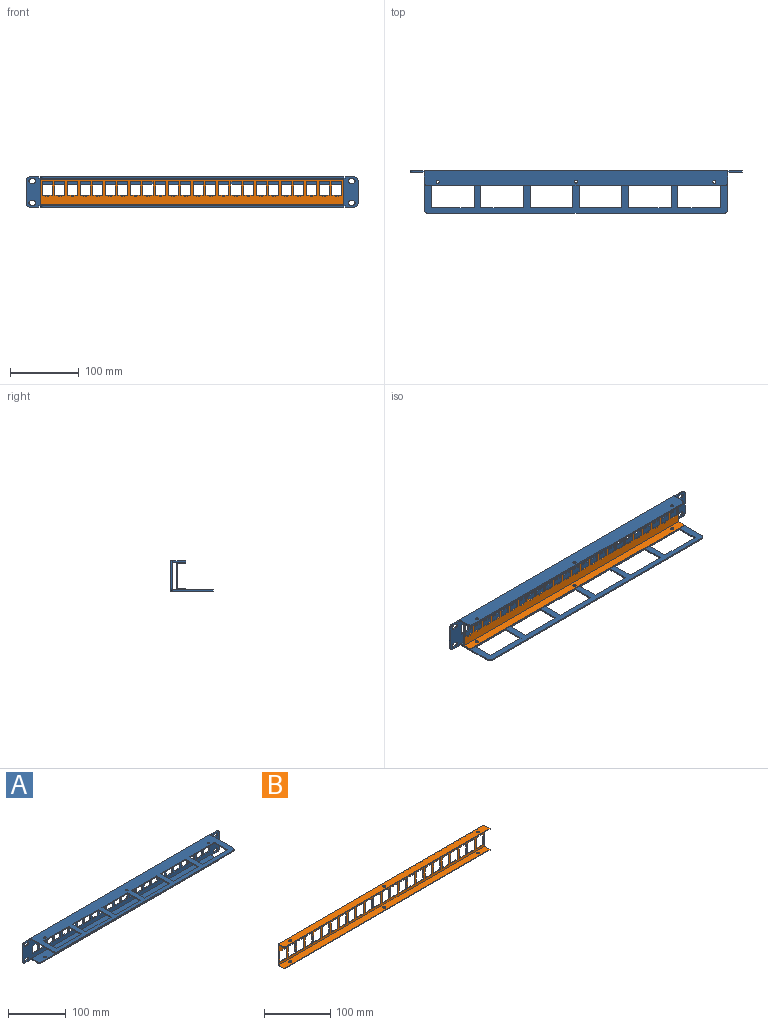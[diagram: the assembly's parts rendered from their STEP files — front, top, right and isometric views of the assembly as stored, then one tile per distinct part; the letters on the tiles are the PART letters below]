
ASSEMBLY  parts=2 mates=1
PART A: 176 faces, bbox 482.7x62x43.8 mm
  f0: plane 440.9x62mm, normal (0,0,1), area 15373.4mm2, adj f86,f87,f134,f143,f144,f145,f146,f147
  f1: plane 440.9x60mm, normal (0,0,-1), area 14491.6mm2, adj f2,f86,f87,f143,f144,f145,f146,f147
  f2: plane 482.7x43.8mm, normal (0,-1,0), area 13415.8mm2, adj f1,f3,f4,f5,f6,f7,f8,f9
  f3: plane 14.65x2mm, normal (0,0,-1), area 29.3mm2, adj f2,f4,f133,f134
  f4: plane 16.2x2mm, normal (-1,0,0), area 32.4mm2, adj f2,f3,f5,f134
  f5: plane 14.65x2mm, normal (0,0,1), area 29.3mm2, adj f2,f4,f133,f134
  f6: plane 14.65x2mm, normal (0,0,-1), area 29.3mm2, adj f2,f7,f105,f134
  f7: plane 16.2x2mm, normal (-1,0,0), area 32.4mm2, adj f2,f6,f8,f134
  f8: plane 14.65x2mm, normal (0,0,1), area 29.3mm2, adj f2,f7,f105,f134
  f9: plane 14.65x2mm, normal (0,0,-1), area 29.3mm2, adj f2,f10,f106,f134
  f10: plane 16.2x2mm, normal (-1,0,0), area 32.4mm2, adj f2,f9,f11,f134
  f11: plane 14.65x2mm, normal (0,0,1), area 29.3mm2, adj f2,f10,f106,f134
  f12: plane 14.65x2mm, normal (0,0,-1), area 29.3mm2, adj f2,f13,f107,f134
  f13: plane 16.2x2mm, normal (-1,0,0), area 32.4mm2, adj f2,f12,f14,f134
  f14: plane 14.65x2mm, normal (0,0,1), area 29.3mm2, adj f2,f13,f107,f134
  f15: plane 14.65x2mm, normal (0,0,-1), area 29.3mm2, adj f2,f16,f108,f134
  f16: plane 16.2x2mm, normal (-1,0,0), area 32.4mm2, adj f2,f15,f17,f134
  f17: plane 14.65x2mm, normal (0,0,1), area 29.3mm2, adj f2,f16,f108,f134
  f18: plane 14.65x2mm, normal (0,0,-1), area 29.3mm2, adj f2,f19,f109,f134
  f19: plane 16.2x2mm, normal (-1,0,0), area 32.4mm2, adj f2,f18,f20,f134
  f20: plane 14.65x2mm, normal (0,0,1), area 29.3mm2, adj f2,f19,f109,f134
  f21: plane 14.65x2mm, normal (0,0,-1), area 29.3mm2, adj f2,f22,f110,f134
  f22: plane 16.2x2mm, normal (-1,0,0), area 32.4mm2, adj f2,f21,f23,f134
  f23: plane 14.65x2mm, normal (0,0,1), area 29.3mm2, adj f2,f22,f110,f134
  f24: plane 14.65x2mm, normal (0,0,-1), area 29.3mm2, adj f2,f25,f111,f134
  f25: plane 16.2x2mm, normal (-1,0,0), area 32.4mm2, adj f2,f24,f26,f134
  f26: plane 14.65x2mm, normal (0,0,1), area 29.3mm2, adj f2,f25,f111,f134
  f27: plane 14.65x2mm, normal (0,0,-1), area 29.3mm2, adj f2,f28,f112,f134
  f28: plane 16.2x2mm, normal (-1,0,0), area 32.4mm2, adj f2,f27,f29,f134
  f29: plane 14.65x2mm, normal (0,0,1), area 29.3mm2, adj f2,f28,f112,f134
  f30: plane 14.65x2mm, normal (0,0,-1), area 29.3mm2, adj f2,f31,f113,f134
  f31: plane 16.2x2mm, normal (-1,0,0), area 32.4mm2, adj f2,f30,f32,f134
  f32: plane 14.65x2mm, normal (0,0,1), area 29.3mm2, adj f2,f31,f113,f134
  f33: plane 14.65x2mm, normal (0,0,-1), area 29.3mm2, adj f2,f34,f114,f134
  f34: plane 16.2x2mm, normal (-1,0,0), area 32.4mm2, adj f2,f33,f35,f134
  f35: plane 14.65x2mm, normal (0,0,1), area 29.3mm2, adj f2,f34,f114,f134
  f36: plane 14.65x2mm, normal (0,0,-1), area 29.3mm2, adj f2,f37,f115,f134
  f37: plane 16.2x2mm, normal (-1,0,0), area 32.4mm2, adj f2,f36,f38,f134
  f38: plane 14.65x2mm, normal (0,0,1), area 29.3mm2, adj f2,f37,f115,f134
  f39: plane 14.65x2mm, normal (0,0,-1), area 29.3mm2, adj f2,f40,f116,f134
  f40: plane 16.2x2mm, normal (-1,0,0), area 32.4mm2, adj f2,f39,f41,f134
  f41: plane 14.65x2mm, normal (0,0,1), area 29.3mm2, adj f2,f40,f116,f134
  f42: plane 14.65x2mm, normal (0,0,-1), area 29.3mm2, adj f2,f43,f117,f134
  f43: plane 16.2x2mm, normal (-1,0,0), area 32.4mm2, adj f2,f42,f44,f134
  f44: plane 14.65x2mm, normal (0,0,1), area 29.3mm2, adj f2,f43,f117,f134
  f45: plane 14.65x2mm, normal (0,0,-1), area 29.3mm2, adj f2,f46,f118,f134
  f46: plane 16.2x2mm, normal (-1,0,0), area 32.4mm2, adj f2,f45,f47,f134
  f47: plane 14.65x2mm, normal (0,0,1), area 29.3mm2, adj f2,f46,f118,f134
  f48: plane 14.65x2mm, normal (0,0,-1), area 29.3mm2, adj f2,f49,f119,f134
  f49: plane 16.2x2mm, normal (-1,0,0), area 32.4mm2, adj f2,f48,f50,f134
  f50: plane 14.65x2mm, normal (0,0,1), area 29.3mm2, adj f2,f49,f119,f134
  f51: plane 14.65x2mm, normal (0,0,-1), area 29.3mm2, adj f2,f52,f120,f134
  f52: plane 16.2x2mm, normal (-1,0,0), area 32.4mm2, adj f2,f51,f53,f134
  f53: plane 14.65x2mm, normal (0,0,1), area 29.3mm2, adj f2,f52,f120,f134
  f54: plane 14.65x2mm, normal (0,0,-1), area 29.3mm2, adj f2,f55,f121,f134
  f55: plane 16.2x2mm, normal (-1,0,0), area 32.4mm2, adj f2,f54,f56,f134
  f56: plane 14.65x2mm, normal (0,0,1), area 29.3mm2, adj f2,f55,f121,f134
  f57: plane 14.65x2mm, normal (0,0,-1), area 29.3mm2, adj f2,f58,f122,f134
  f58: plane 16.2x2mm, normal (-1,0,0), area 32.4mm2, adj f2,f57,f59,f134
  f59: plane 14.65x2mm, normal (0,0,1), area 29.3mm2, adj f2,f58,f122,f134
  f60: plane 14.65x2mm, normal (0,0,-1), area 29.3mm2, adj f2,f61,f123,f134
  f61: plane 16.2x2mm, normal (-1,0,0), area 32.4mm2, adj f2,f60,f62,f134
  f62: plane 14.65x2mm, normal (0,0,1), area 29.3mm2, adj f2,f61,f123,f134
  f63: plane 14.65x2mm, normal (0,0,-1), area 29.3mm2, adj f2,f64,f124,f134
  f64: plane 16.2x2mm, normal (-1,0,0), area 32.4mm2, adj f2,f63,f65,f134
  f65: plane 14.65x2mm, normal (0,0,1), area 29.3mm2, adj f2,f64,f124,f134
  f66: plane 14.65x2mm, normal (0,0,-1), area 29.3mm2, adj f2,f67,f125,f134
  f67: plane 16.2x2mm, normal (-1,0,0), area 32.4mm2, adj f2,f66,f68,f134
  f68: plane 14.65x2mm, normal (0,0,1), area 29.3mm2, adj f2,f67,f125,f134
  f69: plane 14.65x2mm, normal (0,0,-1), area 29.3mm2, adj f2,f70,f126,f134
  f70: plane 16.2x2mm, normal (-1,0,0), area 32.4mm2, adj f2,f69,f71,f134
  f71: plane 14.65x2mm, normal (0,0,1), area 29.3mm2, adj f2,f70,f126,f134
  f72: plane 16.2x2mm, normal (-1,0,0), area 32.4mm2, adj f2,f73,f127,f134
  f73: plane 14.65x2mm, normal (0,0,1), area 29.3mm2, adj f2,f72,f74,f134
  f74: plane 16.2x2mm, normal (1,0,0), area 32.4mm2, adj f2,f73,f127,f134
  f75: cylinder r=3.35mm len=6.7mm, axis (0,-1,0), area 21mm2, adj f2,f76,f128,f134
  f76: plane 3.3x2mm, normal (0,0,-1), area 6.6mm2, adj f2,f75,f77,f134
  f77: cylinder r=3.35mm len=6.7mm, axis (0,-1,0), area 21mm2, adj f2,f76,f128,f134
  f78: cylinder r=3.35mm len=6.7mm, axis (0,-1,0), area 21mm2, adj f2,f79,f129,f134
  f79: plane 3.3x2mm, normal (0,0,-1), area 6.6mm2, adj f2,f78,f80,f134
  f80: cylinder r=3.35mm len=6.7mm, axis (0,-1,0), area 21mm2, adj f2,f79,f129,f134
  f81: plane 13.9x2mm, normal (0,0,-1), area 27.8mm2, adj f2,f130,f134,f139
  f82: plane 33.8x2mm, normal (1,0,0), area 67.6mm2, adj f2,f134,f139,f140
  f83: plane 13.9x2mm, normal (0,0,1), area 27.8mm2, adj f2,f84,f134,f140
  f84: plane 2x2mm, normal (-1,0,0), area 4mm2, adj f2,f83,f85,f134
  f85: plane 2x2mm, normal (0,0,1), area 4mm2, adj f2,f84,f86,f134
  f86: plane 57x2mm, normal (1,0,0), area 114mm2, adj f0,f1,f85,f134,f145
  f87: plane 57x2mm, normal (-1,0,0), area 114mm2, adj f0,f1,f88,f134,f144
  f88: plane 2x2mm, normal (0,0,1), area 4mm2, adj f2,f87,f89,f134
  f89: plane 2x2mm, normal (1,0,0), area 4mm2, adj f2,f88,f90,f134
  f90: plane 13.9x2mm, normal (0,0,1), area 27.8mm2, adj f2,f89,f134,f141
  f91: plane 33.8x2mm, normal (-1,0,0), area 67.6mm2, adj f2,f134,f141,f142
  f92: plane 13.9x2mm, normal (0,0,-1), area 27.8mm2, adj f2,f93,f134,f142
  f93: plane 2x2mm, normal (1,0,0), area 4mm2, adj f2,f92,f94,f134
  f94: plane 2x2mm, normal (0,0,-1), area 4mm2, adj f2,f93,f95,f134
  f95: plane 17x2mm, normal (-1,0,0), area 34mm2, adj f94,f96,f134,f135,f137
  f96: plane 440.9x22mm, normal (0,0,-1), area 9641.4mm2, adj f95,f97,f134,f136,f137,f138,f170,f171
  f97: plane 17x2mm, normal (1,0,0), area 34mm2, adj f96,f98,f134,f135,f138
  f98: plane 2x2mm, normal (0,0,-1), area 4mm2, adj f2,f97,f130,f134
  f99: cylinder r=3.35mm len=6.7mm, axis (0,-1,0), area 21mm2, adj f2,f100,f131,f134
  f100: plane 3.3x2mm, normal (0,0,1), area 6.6mm2, adj f2,f99,f101,f134
  f101: cylinder r=3.35mm len=6.7mm, axis (0,-1,0), area 21mm2, adj f2,f100,f131,f134
  f102: cylinder r=3.35mm len=6.7mm, axis (0,-1,0), area 21mm2, adj f2,f103,f132,f134
  f103: plane 3.3x2mm, normal (0,0,1), area 6.6mm2, adj f2,f102,f104,f134
  f104: cylinder r=3.35mm len=6.7mm, axis (0,-1,0), area 21mm2, adj f2,f103,f132,f134
  f105: plane 16.2x2mm, normal (1,0,0), area 32.4mm2, adj f2,f6,f8,f134
  f106: plane 16.2x2mm, normal (1,0,0), area 32.4mm2, adj f2,f9,f11,f134
  f107: plane 16.2x2mm, normal (1,0,0), area 32.4mm2, adj f2,f12,f14,f134
  f108: plane 16.2x2mm, normal (1,0,0), area 32.4mm2, adj f2,f15,f17,f134
  f109: plane 16.2x2mm, normal (1,0,0), area 32.4mm2, adj f2,f18,f20,f134
  f110: plane 16.2x2mm, normal (1,0,0), area 32.4mm2, adj f2,f21,f23,f134
  f111: plane 16.2x2mm, normal (1,0,0), area 32.4mm2, adj f2,f24,f26,f134
  f112: plane 16.2x2mm, normal (1,0,0), area 32.4mm2, adj f2,f27,f29,f134
  f113: plane 16.2x2mm, normal (1,0,0), area 32.4mm2, adj f2,f30,f32,f134
  f114: plane 16.2x2mm, normal (1,0,0), area 32.4mm2, adj f2,f33,f35,f134
  f115: plane 16.2x2mm, normal (1,0,0), area 32.4mm2, adj f2,f36,f38,f134
  f116: plane 16.2x2mm, normal (1,0,0), area 32.4mm2, adj f2,f39,f41,f134
  f117: plane 16.2x2mm, normal (1,0,0), area 32.4mm2, adj f2,f42,f44,f134
  f118: plane 16.2x2mm, normal (1,0,0), area 32.4mm2, adj f2,f45,f47,f134
  f119: plane 16.2x2mm, normal (1,0,0), area 32.4mm2, adj f2,f48,f50,f134
  f120: plane 16.2x2mm, normal (1,0,0), area 32.4mm2, adj f2,f51,f53,f134
  f121: plane 16.2x2mm, normal (1,0,0), area 32.4mm2, adj f2,f54,f56,f134
  f122: plane 16.2x2mm, normal (1,0,0), area 32.4mm2, adj f2,f57,f59,f134
  f123: plane 16.2x2mm, normal (1,0,0), area 32.4mm2, adj f2,f60,f62,f134
  f124: plane 16.2x2mm, normal (1,0,0), area 32.4mm2, adj f2,f63,f65,f134
  f125: plane 16.2x2mm, normal (1,0,0), area 32.4mm2, adj f2,f66,f68,f134
  f126: plane 16.2x2mm, normal (1,0,0), area 32.4mm2, adj f2,f69,f71,f134
  f127: plane 14.65x2mm, normal (0,0,-1), area 29.3mm2, adj f2,f72,f74,f134
  f128: plane 3.3x2mm, normal (0,0,1), area 6.6mm2, adj f2,f75,f77,f134
  f129: plane 3.3x2mm, normal (0,0,1), area 6.6mm2, adj f2,f78,f80,f134
  f130: plane 2x2mm, normal (-1,0,0), area 4mm2, adj f2,f81,f98,f134
  f131: plane 3.3x2mm, normal (0,0,-1), area 6.6mm2, adj f2,f99,f101,f134
  f132: plane 3.3x2mm, normal (0,0,-1), area 6.6mm2, adj f2,f102,f104,f134
  f133: plane 16.2x2mm, normal (1,0,0), area 32.4mm2, adj f2,f3,f5,f134
  f134: plane 482.7x43.8mm, normal (0,1,0), area 15179.4mm2, adj f0,f3,f4,f5,f6,f7,f8,f9
  f135: plane 440.9x20mm, normal (0,0,1), area 8759.6mm2, adj f2,f95,f97,f136,f137,f138,f170,f171
  f136: plane 430.9x2mm, normal (0,-1,0), area 861.8mm2, adj f96,f135,f137,f138
  f137: cylinder r=5mm len=5mm, axis (0,0,-1), area 15.7mm2, adj f95,f96,f135,f136
  f138: cylinder r=5mm len=5mm, axis (0,0,1), area 15.7mm2, adj f96,f97,f135,f136
  f139: cylinder r=5mm len=5mm, axis (0,-1,0), area 15.7mm2, adj f2,f81,f82,f134
  f140: cylinder r=5mm len=5mm, axis (0,1,0), area 15.7mm2, adj f2,f82,f83,f134
  f141: cylinder r=5mm len=5mm, axis (0,-1,0), area 15.7mm2, adj f2,f90,f91,f134
  f142: cylinder r=5mm len=5mm, axis (0,1,0), area 15.7mm2, adj f2,f91,f92,f134
  f143: plane 430.9x2mm, normal (0,-1,0), area 861.8mm2, adj f0,f1,f144,f145
  f144: cylinder r=5mm len=5mm, axis (0,0,-1), area 15.7mm2, adj f0,f1,f87,f143
  f145: cylinder r=5mm len=5mm, axis (0,0,1), area 15.7mm2, adj f0,f1,f86,f143
  f146: plane 62x2mm, normal (0,-1,0), area 124mm2, adj f0,f1,f147,f149
  f147: plane 32x2mm, normal (-1,0,0), area 64mm2, adj f0,f1,f146,f148
  f148: plane 62x2mm, normal (0,1,0), area 124mm2, adj f0,f1,f147,f149
  f149: plane 32x2mm, normal (1,0,0), area 64mm2, adj f0,f1,f146,f148
  f150: plane 62x2mm, normal (0,-1,0), area 124mm2, adj f0,f1,f151,f153
  f151: plane 32x2mm, normal (-1,0,0), area 64mm2, adj f0,f1,f150,f152
  f152: plane 62x2mm, normal (0,1,0), area 124mm2, adj f0,f1,f151,f153
  f153: plane 32x2mm, normal (1,0,0), area 64mm2, adj f0,f1,f150,f152
  f154: plane 62x2mm, normal (0,-1,0), area 124mm2, adj f0,f1,f155,f157
  f155: plane 32x2mm, normal (-1,0,0), area 64mm2, adj f0,f1,f154,f156
  f156: plane 62x2mm, normal (0,1,0), area 124mm2, adj f0,f1,f155,f157
  f157: plane 32x2mm, normal (1,0,0), area 64mm2, adj f0,f1,f154,f156
  f158: plane 62x2mm, normal (0,-1,0), area 124mm2, adj f0,f1,f159,f161
  f159: plane 32x2mm, normal (-1,0,0), area 64mm2, adj f0,f1,f158,f160
  f160: plane 62x2mm, normal (0,1,0), area 124mm2, adj f0,f1,f159,f161
  f161: plane 32x2mm, normal (1,0,0), area 64mm2, adj f0,f1,f158,f160
  f162: plane 62x2mm, normal (0,-1,0), area 124mm2, adj f0,f1,f163,f165
  f163: plane 32x2mm, normal (-1,0,0), area 64mm2, adj f0,f1,f162,f164
  f164: plane 62x2mm, normal (0,1,0), area 124mm2, adj f0,f1,f163,f165
  f165: plane 32x2mm, normal (1,0,0), area 64mm2, adj f0,f1,f162,f164
  f166: plane 62x2mm, normal (0,-1,0), area 124mm2, adj f0,f1,f167,f169
  f167: plane 32x2mm, normal (-1,0,0), area 64mm2, adj f0,f1,f166,f168
  f168: plane 62x2mm, normal (0,1,0), area 124mm2, adj f0,f1,f167,f169
  f169: plane 32x2mm, normal (1,0,0), area 64mm2, adj f0,f1,f166,f168
  f170: cylinder r=2.25mm len=4.5mm, axis (0,0,1), area 28.3mm2, adj f96,f135
  f171: cylinder r=2.25mm len=4.5mm, axis (0,0,1), area 28.3mm2, adj f96,f135
  f172: cylinder r=2.25mm len=4.5mm, axis (0,0,1), area 28.3mm2, adj f96,f135
  f173: cylinder r=2.25mm len=4.5mm, axis (0,0,1), area 28.3mm2, adj f0,f1
  f174: cylinder r=2.25mm len=4.5mm, axis (0,0,1), area 28.3mm2, adj f0,f1
  f175: cylinder r=2.25mm len=4.5mm, axis (0,0,1), area 28.3mm2, adj f0,f1
PART B: 209 faces, bbox 440.9x13x39.8 mm
  f0: plane 440.9x37.8mm, normal (0,-1,0), area 9613.1mm2, adj f1,f2,f3,f4,f5,f6,f7,f8
  f1: plane 4x1mm, normal (0,0,-1), area 4mm2, adj f0,f2,f196,f197
  f2: plane 1.5x1mm, normal (-1,0,0), area 1.5mm2, adj f0,f1,f3,f197
  f3: plane 5.33x1mm, normal (0,0,-1), area 5.3mm2, adj f0,f2,f4,f197
  f4: plane 19.65x1mm, normal (-1,0,0), area 19.7mm2, adj f0,f3,f5,f197
  f5: plane 14.65x1mm, normal (0,0,1), area 14.6mm2, adj f0,f4,f6,f197
  f6: plane 19.65x1mm, normal (1,0,0), area 19.7mm2, adj f0,f5,f7,f197
  f7: plane 5.33x1mm, normal (0,0,-1), area 5.3mm2, adj f0,f6,f196,f197
  f8: plane 5.33x1mm, normal (0,0,-1), area 5.3mm2, adj f0,f9,f172,f197
  f9: plane 1.5x1mm, normal (1,0,0), area 1.5mm2, adj f0,f8,f10,f197
  f10: plane 4x1mm, normal (0,0,-1), area 4mm2, adj f0,f9,f11,f197
  f11: plane 1.5x1mm, normal (-1,0,0), area 1.5mm2, adj f0,f10,f12,f197
  f12: plane 5.33x1mm, normal (0,0,-1), area 5.3mm2, adj f0,f11,f13,f197
  f13: plane 19.65x1mm, normal (-1,0,0), area 19.7mm2, adj f0,f12,f14,f197
  f14: plane 14.65x1mm, normal (0,0,1), area 14.6mm2, adj f0,f13,f172,f197
  f15: plane 5.33x1mm, normal (0,0,-1), area 5.3mm2, adj f0,f16,f173,f197
  f16: plane 1.5x1mm, normal (1,0,0), area 1.5mm2, adj f0,f15,f17,f197
  f17: plane 4x1mm, normal (0,0,-1), area 4mm2, adj f0,f16,f18,f197
  f18: plane 1.5x1mm, normal (-1,0,0), area 1.5mm2, adj f0,f17,f19,f197
  f19: plane 5.33x1mm, normal (0,0,-1), area 5.3mm2, adj f0,f18,f20,f197
  f20: plane 19.65x1mm, normal (-1,0,0), area 19.7mm2, adj f0,f19,f21,f197
  f21: plane 14.65x1mm, normal (0,0,1), area 14.6mm2, adj f0,f20,f173,f197
  f22: plane 5.33x1mm, normal (0,0,-1), area 5.3mm2, adj f0,f23,f174,f197
  f23: plane 1.5x1mm, normal (1,0,0), area 1.5mm2, adj f0,f22,f24,f197
  f24: plane 4x1mm, normal (0,0,-1), area 4mm2, adj f0,f23,f25,f197
  f25: plane 1.5x1mm, normal (-1,0,0), area 1.5mm2, adj f0,f24,f26,f197
  f26: plane 5.33x1mm, normal (0,0,-1), area 5.3mm2, adj f0,f25,f27,f197
  f27: plane 19.65x1mm, normal (-1,0,0), area 19.7mm2, adj f0,f26,f28,f197
  f28: plane 14.65x1mm, normal (0,0,1), area 14.6mm2, adj f0,f27,f174,f197
  f29: plane 5.33x1mm, normal (0,0,-1), area 5.3mm2, adj f0,f30,f175,f197
  f30: plane 1.5x1mm, normal (1,0,0), area 1.5mm2, adj f0,f29,f31,f197
  f31: plane 4x1mm, normal (0,0,-1), area 4mm2, adj f0,f30,f32,f197
  f32: plane 1.5x1mm, normal (-1,0,0), area 1.5mm2, adj f0,f31,f33,f197
  f33: plane 5.33x1mm, normal (0,0,-1), area 5.3mm2, adj f0,f32,f34,f197
  f34: plane 19.65x1mm, normal (-1,0,0), area 19.7mm2, adj f0,f33,f35,f197
  f35: plane 14.65x1mm, normal (0,0,1), area 14.6mm2, adj f0,f34,f175,f197
  f36: plane 5.33x1mm, normal (0,0,-1), area 5.3mm2, adj f0,f37,f176,f197
  f37: plane 1.5x1mm, normal (1,0,0), area 1.5mm2, adj f0,f36,f38,f197
  f38: plane 4x1mm, normal (0,0,-1), area 4mm2, adj f0,f37,f39,f197
  f39: plane 1.5x1mm, normal (-1,0,0), area 1.5mm2, adj f0,f38,f40,f197
  f40: plane 5.33x1mm, normal (0,0,-1), area 5.3mm2, adj f0,f39,f41,f197
  f41: plane 19.65x1mm, normal (-1,0,0), area 19.7mm2, adj f0,f40,f42,f197
  f42: plane 14.65x1mm, normal (0,0,1), area 14.6mm2, adj f0,f41,f176,f197
  f43: plane 5.33x1mm, normal (0,0,-1), area 5.3mm2, adj f0,f44,f177,f197
  f44: plane 1.5x1mm, normal (1,0,0), area 1.5mm2, adj f0,f43,f45,f197
  f45: plane 4x1mm, normal (0,0,-1), area 4mm2, adj f0,f44,f46,f197
  f46: plane 1.5x1mm, normal (-1,0,0), area 1.5mm2, adj f0,f45,f47,f197
  f47: plane 5.33x1mm, normal (0,0,-1), area 5.3mm2, adj f0,f46,f48,f197
  f48: plane 19.65x1mm, normal (-1,0,0), area 19.7mm2, adj f0,f47,f49,f197
  f49: plane 14.65x1mm, normal (0,0,1), area 14.6mm2, adj f0,f48,f177,f197
  f50: plane 5.33x1mm, normal (0,0,-1), area 5.3mm2, adj f0,f51,f178,f197
  f51: plane 1.5x1mm, normal (1,0,0), area 1.5mm2, adj f0,f50,f52,f197
  f52: plane 4x1mm, normal (0,0,-1), area 4mm2, adj f0,f51,f53,f197
  f53: plane 1.5x1mm, normal (-1,0,0), area 1.5mm2, adj f0,f52,f54,f197
  f54: plane 5.33x1mm, normal (0,0,-1), area 5.3mm2, adj f0,f53,f55,f197
  f55: plane 19.65x1mm, normal (-1,0,0), area 19.7mm2, adj f0,f54,f56,f197
  f56: plane 14.65x1mm, normal (0,0,1), area 14.6mm2, adj f0,f55,f178,f197
  f57: plane 5.33x1mm, normal (0,0,-1), area 5.3mm2, adj f0,f58,f179,f197
  f58: plane 1.5x1mm, normal (1,0,0), area 1.5mm2, adj f0,f57,f59,f197
  f59: plane 4x1mm, normal (0,0,-1), area 4mm2, adj f0,f58,f60,f197
  f60: plane 1.5x1mm, normal (-1,0,0), area 1.5mm2, adj f0,f59,f61,f197
  f61: plane 5.33x1mm, normal (0,0,-1), area 5.3mm2, adj f0,f60,f62,f197
  f62: plane 19.65x1mm, normal (-1,0,0), area 19.7mm2, adj f0,f61,f63,f197
  f63: plane 14.65x1mm, normal (0,0,1), area 14.7mm2, adj f0,f62,f179,f197
  f64: plane 5.33x1mm, normal (0,0,-1), area 5.3mm2, adj f0,f65,f180,f197
  f65: plane 1.5x1mm, normal (1,0,0), area 1.5mm2, adj f0,f64,f66,f197
  f66: plane 4x1mm, normal (0,0,-1), area 4mm2, adj f0,f65,f67,f197
  f67: plane 1.5x1mm, normal (-1,0,0), area 1.5mm2, adj f0,f66,f68,f197
  f68: plane 5.33x1mm, normal (0,0,-1), area 5.3mm2, adj f0,f67,f69,f197
  f69: plane 19.65x1mm, normal (-1,0,0), area 19.7mm2, adj f0,f68,f70,f197
  f70: plane 14.65x1mm, normal (0,0,1), area 14.7mm2, adj f0,f69,f180,f197
  f71: plane 5.33x1mm, normal (0,0,-1), area 5.3mm2, adj f0,f72,f181,f197
  f72: plane 1.5x1mm, normal (1,0,0), area 1.5mm2, adj f0,f71,f73,f197
  f73: plane 4x1mm, normal (0,0,-1), area 4mm2, adj f0,f72,f74,f197
  f74: plane 1.5x1mm, normal (-1,0,0), area 1.5mm2, adj f0,f73,f75,f197
  f75: plane 5.33x1mm, normal (0,0,-1), area 5.3mm2, adj f0,f74,f76,f197
  f76: plane 19.65x1mm, normal (-1,0,0), area 19.7mm2, adj f0,f75,f77,f197
  f77: plane 14.65x1mm, normal (0,0,1), area 14.7mm2, adj f0,f76,f181,f197
  f78: plane 5.33x1mm, normal (0,0,-1), area 5.3mm2, adj f0,f79,f182,f197
  f79: plane 1.5x1mm, normal (1,0,0), area 1.5mm2, adj f0,f78,f80,f197
  f80: plane 4x1mm, normal (0,0,-1), area 4mm2, adj f0,f79,f81,f197
  f81: plane 1.5x1mm, normal (-1,0,0), area 1.5mm2, adj f0,f80,f82,f197
  f82: plane 5.33x1mm, normal (0,0,-1), area 5.3mm2, adj f0,f81,f83,f197
  f83: plane 19.65x1mm, normal (-1,0,0), area 19.7mm2, adj f0,f82,f84,f197
  f84: plane 14.65x1mm, normal (0,0,1), area 14.6mm2, adj f0,f83,f182,f197
  f85: plane 5.33x1mm, normal (0,0,-1), area 5.3mm2, adj f0,f86,f183,f197
  f86: plane 1.5x1mm, normal (1,0,0), area 1.5mm2, adj f0,f85,f87,f197
  f87: plane 4x1mm, normal (0,0,-1), area 4mm2, adj f0,f86,f88,f197
  f88: plane 1.5x1mm, normal (-1,0,0), area 1.5mm2, adj f0,f87,f89,f197
  f89: plane 5.33x1mm, normal (0,0,-1), area 5.3mm2, adj f0,f88,f90,f197
  f90: plane 19.65x1mm, normal (-1,0,0), area 19.7mm2, adj f0,f89,f91,f197
  f91: plane 14.65x1mm, normal (0,0,1), area 14.6mm2, adj f0,f90,f183,f197
  f92: plane 5.33x1mm, normal (0,0,-1), area 5.3mm2, adj f0,f93,f184,f197
  f93: plane 1.5x1mm, normal (1,0,0), area 1.5mm2, adj f0,f92,f94,f197
  f94: plane 4x1mm, normal (0,0,-1), area 4mm2, adj f0,f93,f95,f197
  f95: plane 1.5x1mm, normal (-1,0,0), area 1.5mm2, adj f0,f94,f96,f197
  f96: plane 5.33x1mm, normal (0,0,-1), area 5.3mm2, adj f0,f95,f97,f197
  f97: plane 19.65x1mm, normal (-1,0,0), area 19.7mm2, adj f0,f96,f98,f197
  f98: plane 14.65x1mm, normal (0,0,1), area 14.6mm2, adj f0,f97,f184,f197
  f99: plane 5.33x1mm, normal (0,0,-1), area 5.3mm2, adj f0,f100,f185,f197
  f100: plane 1.5x1mm, normal (1,0,0), area 1.5mm2, adj f0,f99,f101,f197
  f101: plane 4x1mm, normal (0,0,-1), area 4mm2, adj f0,f100,f102,f197
  f102: plane 1.5x1mm, normal (-1,0,0), area 1.5mm2, adj f0,f101,f103,f197
  f103: plane 5.33x1mm, normal (0,0,-1), area 5.3mm2, adj f0,f102,f104,f197
  f104: plane 19.65x1mm, normal (-1,0,0), area 19.7mm2, adj f0,f103,f105,f197
  f105: plane 14.65x1mm, normal (0,0,1), area 14.6mm2, adj f0,f104,f185,f197
  f106: plane 5.33x1mm, normal (0,0,-1), area 5.3mm2, adj f0,f107,f186,f197
  f107: plane 1.5x1mm, normal (1,0,0), area 1.5mm2, adj f0,f106,f108,f197
  f108: plane 4x1mm, normal (0,0,-1), area 4mm2, adj f0,f107,f109,f197
  f109: plane 1.5x1mm, normal (-1,0,0), area 1.5mm2, adj f0,f108,f110,f197
  f110: plane 5.33x1mm, normal (0,0,-1), area 5.3mm2, adj f0,f109,f111,f197
  f111: plane 19.65x1mm, normal (-1,0,0), area 19.7mm2, adj f0,f110,f112,f197
  f112: plane 14.65x1mm, normal (0,0,1), area 14.7mm2, adj f0,f111,f186,f197
  f113: plane 5.33x1mm, normal (0,0,-1), area 5.3mm2, adj f0,f114,f187,f197
  f114: plane 1.5x1mm, normal (1,0,0), area 1.5mm2, adj f0,f113,f115,f197
  f115: plane 4x1mm, normal (0,0,-1), area 4mm2, adj f0,f114,f116,f197
  f116: plane 1.5x1mm, normal (-1,0,0), area 1.5mm2, adj f0,f115,f117,f197
  f117: plane 5.33x1mm, normal (0,0,-1), area 5.3mm2, adj f0,f116,f118,f197
  f118: plane 19.65x1mm, normal (-1,0,0), area 19.7mm2, adj f0,f117,f119,f197
  f119: plane 14.65x1mm, normal (0,0,1), area 14.7mm2, adj f0,f118,f187,f197
  f120: plane 5.33x1mm, normal (0,0,-1), area 5.3mm2, adj f0,f121,f188,f197
  f121: plane 1.5x1mm, normal (1,0,0), area 1.5mm2, adj f0,f120,f122,f197
  f122: plane 4x1mm, normal (0,0,-1), area 4mm2, adj f0,f121,f123,f197
  f123: plane 1.5x1mm, normal (-1,0,0), area 1.5mm2, adj f0,f122,f124,f197
  f124: plane 5.33x1mm, normal (0,0,-1), area 5.3mm2, adj f0,f123,f125,f197
  f125: plane 19.65x1mm, normal (-1,0,0), area 19.7mm2, adj f0,f124,f126,f197
  f126: plane 14.65x1mm, normal (0,0,1), area 14.7mm2, adj f0,f125,f188,f197
  f127: plane 5.33x1mm, normal (0,0,-1), area 5.3mm2, adj f0,f128,f189,f197
  f128: plane 1.5x1mm, normal (1,0,0), area 1.5mm2, adj f0,f127,f129,f197
  f129: plane 4x1mm, normal (0,0,-1), area 4mm2, adj f0,f128,f130,f197
  f130: plane 1.5x1mm, normal (-1,0,0), area 1.5mm2, adj f0,f129,f131,f197
  f131: plane 5.33x1mm, normal (0,0,-1), area 5.3mm2, adj f0,f130,f132,f197
  f132: plane 19.65x1mm, normal (-1,0,0), area 19.7mm2, adj f0,f131,f133,f197
  f133: plane 14.65x1mm, normal (0,0,1), area 14.6mm2, adj f0,f132,f189,f197
  f134: plane 5.33x1mm, normal (0,0,-1), area 5.3mm2, adj f0,f135,f190,f197
  f135: plane 1.5x1mm, normal (1,0,0), area 1.5mm2, adj f0,f134,f136,f197
  f136: plane 4x1mm, normal (0,0,-1), area 4mm2, adj f0,f135,f137,f197
  f137: plane 1.5x1mm, normal (-1,0,0), area 1.5mm2, adj f0,f136,f138,f197
  f138: plane 5.33x1mm, normal (0,0,-1), area 5.3mm2, adj f0,f137,f139,f197
  f139: plane 19.65x1mm, normal (-1,0,0), area 19.7mm2, adj f0,f138,f140,f197
  f140: plane 14.65x1mm, normal (0,0,1), area 14.6mm2, adj f0,f139,f190,f197
  f141: plane 5.33x1mm, normal (0,0,-1), area 5.3mm2, adj f0,f142,f191,f197
  f142: plane 1.5x1mm, normal (1,0,0), area 1.5mm2, adj f0,f141,f143,f197
  f143: plane 4x1mm, normal (0,0,-1), area 4mm2, adj f0,f142,f144,f197
  f144: plane 1.5x1mm, normal (-1,0,0), area 1.5mm2, adj f0,f143,f145,f197
  f145: plane 5.33x1mm, normal (0,0,-1), area 5.3mm2, adj f0,f144,f146,f197
  f146: plane 19.65x1mm, normal (-1,0,0), area 19.7mm2, adj f0,f145,f147,f197
  f147: plane 14.65x1mm, normal (0,0,1), area 14.6mm2, adj f0,f146,f191,f197
  f148: plane 5.33x1mm, normal (0,0,-1), area 5.3mm2, adj f0,f149,f192,f197
  f149: plane 1.5x1mm, normal (1,0,0), area 1.5mm2, adj f0,f148,f150,f197
  f150: plane 4x1mm, normal (0,0,-1), area 4mm2, adj f0,f149,f151,f197
  f151: plane 1.5x1mm, normal (-1,0,0), area 1.5mm2, adj f0,f150,f152,f197
  f152: plane 5.33x1mm, normal (0,0,-1), area 5.3mm2, adj f0,f151,f153,f197
  f153: plane 19.65x1mm, normal (-1,0,0), area 19.7mm2, adj f0,f152,f154,f197
  f154: plane 14.65x1mm, normal (0,0,1), area 14.6mm2, adj f0,f153,f192,f197
  f155: plane 5.33x1mm, normal (0,0,-1), area 5.3mm2, adj f0,f156,f193,f197
  f156: plane 1.5x1mm, normal (1,0,0), area 1.5mm2, adj f0,f155,f157,f197
  f157: plane 4x1mm, normal (0,0,-1), area 4mm2, adj f0,f156,f158,f197
  f158: plane 1.5x1mm, normal (-1,0,0), area 1.5mm2, adj f0,f157,f159,f197
  f159: plane 5.33x1mm, normal (0,0,-1), area 5.3mm2, adj f0,f158,f160,f197
  f160: plane 19.65x1mm, normal (-1,0,0), area 19.7mm2, adj f0,f159,f161,f197
  f161: plane 14.65x1mm, normal (0,0,1), area 14.6mm2, adj f0,f160,f193,f197
  f162: plane 5.33x1mm, normal (0,0,-1), area 5.3mm2, adj f0,f163,f194,f197
  f163: plane 1.5x1mm, normal (1,0,0), area 1.5mm2, adj f0,f162,f164,f197
  f164: plane 4x1mm, normal (0,0,-1), area 4mm2, adj f0,f163,f165,f197
  f165: plane 1.5x1mm, normal (-1,0,0), area 1.5mm2, adj f0,f164,f166,f197
  f166: plane 5.33x1mm, normal (0,0,-1), area 5.3mm2, adj f0,f165,f167,f197
  f167: plane 19.65x1mm, normal (-1,0,0), area 19.7mm2, adj f0,f166,f168,f197
  f168: plane 14.65x1mm, normal (0,0,1), area 14.6mm2, adj f0,f167,f194,f197
  f169: plane 39.8x13mm, normal (1,0,0), area 63.8mm2, adj f0,f170,f195,f197,f198,f199,f200,f201
  f170: plane 440.9x13mm, normal (0,0,1), area 5682.1mm2, adj f169,f171,f197,f199,f202,f206,f207,f208
  f171: plane 39.8x13mm, normal (-1,0,0), area 60.8mm2, adj f0,f170,f195,f197,f198,f200,f201,f202
  f172: plane 19.65x1mm, normal (1,0,0), area 19.7mm2, adj f0,f8,f14,f197
  f173: plane 19.65x1mm, normal (1,0,0), area 19.7mm2, adj f0,f15,f21,f197
  f174: plane 19.65x1mm, normal (1,0,0), area 19.7mm2, adj f0,f22,f28,f197
  f175: plane 19.65x1mm, normal (1,0,0), area 19.7mm2, adj f0,f29,f35,f197
  f176: plane 19.65x1mm, normal (1,0,0), area 19.7mm2, adj f0,f36,f42,f197
  f177: plane 19.65x1mm, normal (1,0,0), area 19.7mm2, adj f0,f43,f49,f197
  f178: plane 19.65x1mm, normal (1,0,0), area 19.7mm2, adj f0,f50,f56,f197
  f179: plane 19.65x1mm, normal (1,0,0), area 19.7mm2, adj f0,f57,f63,f197
  f180: plane 19.65x1mm, normal (1,0,0), area 19.7mm2, adj f0,f64,f70,f197
  f181: plane 19.65x1mm, normal (1,0,0), area 19.7mm2, adj f0,f71,f77,f197
  f182: plane 19.65x1mm, normal (1,0,0), area 19.7mm2, adj f0,f78,f84,f197
  f183: plane 19.65x1mm, normal (1,0,0), area 19.7mm2, adj f0,f85,f91,f197
  f184: plane 19.65x1mm, normal (1,0,0), area 19.7mm2, adj f0,f92,f98,f197
  f185: plane 19.65x1mm, normal (1,0,0), area 19.7mm2, adj f0,f99,f105,f197
  f186: plane 19.65x1mm, normal (1,0,0), area 19.7mm2, adj f0,f106,f112,f197
  f187: plane 19.65x1mm, normal (1,0,0), area 19.7mm2, adj f0,f113,f119,f197
  f188: plane 19.65x1mm, normal (1,0,0), area 19.7mm2, adj f0,f120,f126,f197
  f189: plane 19.65x1mm, normal (1,0,0), area 19.7mm2, adj f0,f127,f133,f197
  f190: plane 19.65x1mm, normal (1,0,0), area 19.7mm2, adj f0,f134,f140,f197
  f191: plane 19.65x1mm, normal (1,0,0), area 19.7mm2, adj f0,f141,f147,f197
  f192: plane 19.65x1mm, normal (1,0,0), area 19.7mm2, adj f0,f148,f154,f197
  f193: plane 19.65x1mm, normal (1,0,0), area 19.7mm2, adj f0,f155,f161,f197
  f194: plane 19.65x1mm, normal (1,0,0), area 19.7mm2, adj f0,f162,f168,f197
  f195: plane 440.9x13mm, normal (0,0,-1), area 5684mm2, adj f169,f171,f197,f201,f203,f204,f205
  f196: plane 1.5x1mm, normal (1,0,0), area 1.5mm2, adj f0,f1,f7,f197
  f197: plane 440.9x39.8mm, normal (0,1,0), area 10494.9mm2, adj f1,f2,f3,f4,f5,f6,f7,f8
  f198: plane 440.9x12mm, normal (0,0,-1), area 5241.2mm2, adj f0,f169,f171,f199,f202,f206,f207,f208
  f199: plane 437.9x1mm, normal (0,-1,0), area 437.9mm2, adj f169,f170,f198,f202
  f200: plane 440.9x12mm, normal (0,0,1), area 5243.1mm2, adj f0,f169,f171,f201,f203,f204,f205
  f201: plane 440.9x1mm, normal (0,-1,0), area 440.9mm2, adj f169,f171,f195,f200
  f202: cylinder r=3mm len=3mm, axis (0,0,1), area 4.7mm2, adj f170,f171,f198,f199
  f203: cylinder r=2.25mm len=4.5mm, axis (0,0,-1), area 14.1mm2, adj f195,f200
  f204: cylinder r=2.25mm len=4.5mm, axis (0,0,-1), area 14.1mm2, adj f195,f200
  f205: cylinder r=2.25mm len=4.5mm, axis (0,0,-1), area 14.1mm2, adj f195,f200
  f206: cylinder r=2.25mm len=4.5mm, axis (0,0,-1), area 14.1mm2, adj f170,f198
  f207: cylinder r=2.25mm len=4.5mm, axis (0,0,-1), area 14.1mm2, adj f170,f198
  f208: cylinder r=2.25mm len=4.5mm, axis (0,0,-1), area 14.1mm2, adj f170,f198
PLACE A rot(axis=(0,1,0),180deg) t=(-1.82,0,-3.2)mm
PLACE B rot(axis=(0,1,0),180deg) t=(-1.82,-7,-3.2)mm
MATE fastened B.f203 <-> A.f170  axis (0,0,1) through (199.41,-14,16.7)mm
